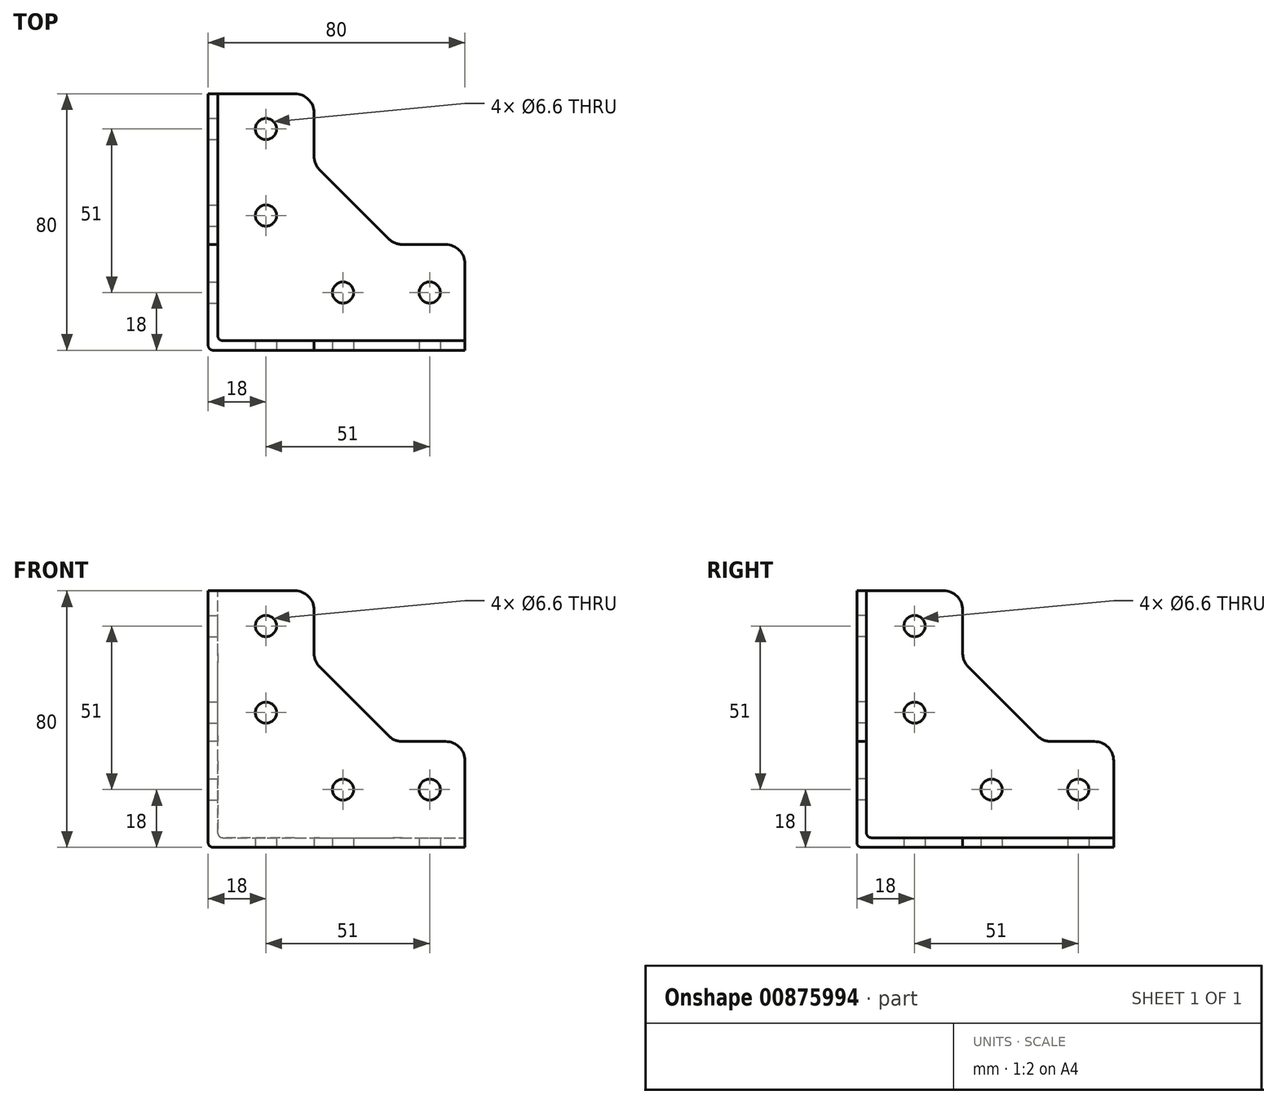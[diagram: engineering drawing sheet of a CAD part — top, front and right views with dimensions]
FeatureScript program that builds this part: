
annotation { "Feature Type Name" : "Feature", "Feature Type Description" : "" }
export const myFeature = defineFeature(function(context is Context, id is Id, definition is map)
    precondition{}
    {
        {
            var Q0;
            Q0=qCreatedBy(makeId("Front.planeOp"),FACE);
            var sketch = newSketch(context, id + "F0", { "sketchPlane" : qUnion([Q0])});
            skLineSegment(sketch, "E0", {"start": v(0, 80) * mm, "end": v(0, 0) * mm});
            skLineSegment(sketch, "E1", {"start": v(0, 0) * mm, "end": v(80, 0) * mm});
            skLineSegment(sketch, "E2", {"start": v(80, 0) * mm, "end": v(80, 33) * mm});
            skLineSegment(sketch, "E3", {"start": v(33, 80) * mm, "end": v(0, 80) * mm});
            skLineSegment(sketch, "E4", {"start": v(80, 33) * mm, "end": v(58, 33) * mm});
            skLineSegment(sketch, "E5", {"start": v(58, 33) * mm, "end": v(33, 58) * mm});
            skLineSegment(sketch, "E6", {"start": v(33, 58) * mm, "end": v(33, 80) * mm});
            skSolve(sketch);
        }
        {
            var Q0;
            Q0 = qSketchRegion(id + "F0", true);
            extrude(context, id + "F1", {"entities" : qUnion([Q0]), "oppositeDirection" : true, "depth" : 3 * mm, "offsetDistance" : 25 * mm});
        }
        {
            var Q0;
            Q0=qCreatedBy(makeId("Right.planeOp"),FACE);
            var sketch = newSketch(context, id + "F2", { "sketchPlane" : qUnion([Q0])});
            skLineSegment(sketch, "E7", {"start": v(0, 0) * mm, "end": v(0, 80) * mm});
            skLineSegment(sketch, "E8", {"start": v(0, 80) * mm, "end": v(33, 80) * mm});
            skLineSegment(sketch, "E9", {"start": v(80, 33) * mm, "end": v(80, 0) * mm});
            skLineSegment(sketch, "E10", {"start": v(80, 0) * mm, "end": v(0, 0) * mm});
            skLineSegment(sketch, "E11", {"start": v(80, 33) * mm, "end": v(58, 33) * mm});
            skLineSegment(sketch, "E12", {"start": v(58, 33) * mm, "end": v(33, 58) * mm});
            skLineSegment(sketch, "E13", {"start": v(33, 58) * mm, "end": v(33, 80) * mm});
            skSolve(sketch);
        }
        {
            var Q0;
            Q0 = qSketchRegion(id + "F2", true);
            extrude(context, id + "F3", {"entities" : qUnion([Q0]), "operationType" : NewBodyOperationType.ADD, "depth" : 3 * mm, "offsetDistance" : 25 * mm});
        }
        {
            var Q0;
            Q0=makeQuery(id+"F3.boolean.opBoolean","MERGE",FACE,{"derivedFrom":[makeQuery(id+"F1.opExtrude","SWEPT_FACE",FACE,{"disambiguationData":[OSD([sQuery(id+"F0.wireOp",EDGE,"E1")])]}),makeQuery(id+"F3.opExtrude","SWEPT_FACE",FACE,{"disambiguationData":[OSD([sQuery(id+"F2.wireOp",EDGE,"xK7a5ISh-bIRp-c4a8-oJV0-LNm0MhKTAAZs")])]})]});
            var sketch = newSketch(context, id + "F4", { "sketchPlane" : qUnion([Q0])});
            skLineSegment(sketch, "E14", {"start": v(0, 0) * mm, "end": v(80, 0) * mm});
            skLineSegment(sketch, "E15", {"start": v(80, 0) * mm, "end": v(80, -33) * mm});
            skLineSegment(sketch, "E16", {"start": v(33, -80) * mm, "end": v(0, -80) * mm});
            skLineSegment(sketch, "E17", {"start": v(0, -80) * mm, "end": v(0, 0) * mm});
            skLineSegment(sketch, "E18", {"start": v(33, -80) * mm, "end": v(33, -58) * mm});
            skLineSegment(sketch, "E19", {"start": v(33, -58) * mm, "end": v(58, -33) * mm});
            skLineSegment(sketch, "E20", {"start": v(58, -33) * mm, "end": v(80, -33) * mm});
            skSolve(sketch);
        }
        {
            var Q0;
            Q0 = qSketchRegion(id + "F4", true);
            extrude(context, id + "F5", {"entities" : qUnion([Q0]), "operationType" : NewBodyOperationType.ADD, "oppositeDirection" : true, "depth" : 3 * mm, "offsetDistance" : 25 * mm});
        }
        {
            var Q0;
            Q0=makeQuery(id+"F1.opExtrude","CAP_FACE",FACE,{"disambiguationData":[OSD([sQuery(id+"F0.wireOp",EDGE,"E0"),sQuery(id+"F0.wireOp",EDGE,"E1"),sQuery(id+"F0.wireOp",EDGE,"E2"),sQuery(id+"F0.wireOp",EDGE,"PdstRRKM-6kGl-S3Kn-xvEP-UkvPPowbuID2"),sQuery(id+"F0.wireOp",EDGE,"E3")])],"isStart":true});
            var sketch = newSketch(context, id + "F6", { "sketchPlane" : qUnion([Q0])});
            skLineSegment(sketch, "E21", {"start": v(80, 18) * mm, "end": v(80, 0) * mm, "construction": true});
            skLineSegment(sketch, "E22", {"start": v(0, 18) * mm, "end": v(42, 18) * mm, "construction": true});
            skLineSegment(sketch, "E23", {"start": v(42, 18) * mm, "end": v(69, 18) * mm, "construction": true});
            skLineSegment(sketch, "E24", {"start": v(69, 18) * mm, "end": v(80, 18) * mm, "construction": true});
            skLineSegment(sketch, "E25", {"start": v(0, 80) * mm, "end": v(18, 80) * mm, "construction": true});
            skLineSegment(sketch, "E26", {"start": v(18, 80) * mm, "end": v(18, 0) * mm, "construction": true});
            skPoint(sketch, "E27", {"position": v(18, 69) * mm});
            skPoint(sketch, "E28", {"position": v(18, 42) * mm});
            skSolve(sketch);
        }
        {
            var Q0;
            Q0=sQuery(id+"F6.wireOp",VERTEX,"E22.end");
            var Q1;
            Q1=sQuery(id+"F6.wireOp",VERTEX,"E23.end");
            var Q2;
            Q2=sQuery(id+"F6.wireOp",VERTEX,"E27");
            var Q3;
            Q3=sQuery(id+"F6.wireOp",VERTEX,"E28");
            var Q4;
            Q4=makeQuery(id+"F1.opExtrude","SWEPT_BODY",BODY,{"disambiguationData":[OSD([sQuery(id+"F0.wireOp",EDGE,"E0"),sQuery(id+"F0.wireOp",EDGE,"E1"),sQuery(id+"F0.wireOp",EDGE,"E2"),sQuery(id+"F0.wireOp",EDGE,"PdstRRKM-6kGl-S3Kn-xvEP-UkvPPowbuID2"),sQuery(id+"F0.wireOp",EDGE,"E3")])]});
            hole(context, id + "F7", {"style" : HoleStyle.SIMPLE, "endStyle" : HoleEndStyle.THROUGH, "standardTappedOrClearance" : lookupTablePath({ "fit" : "Normal", "standard" : "ISO", "size" : "M6", "type" : "Clearance" }), "standardBlindInLast" : lookupTablePath({ "fit" : "Normal", "standard" : "ISO", "size" : "M6", "type" : "Clearance" }), "holeDiameter" : 6.6 * mm, "majorDiameter" : 5 * mm, "isTappedThrough" : true, "tappedDepth" : 18.5 * mm, "tapClearance" : 3, "locations" : qUnion([Q0, Q1, Q2, Q3]), "scope" : qUnion([Q4])});
        }
        {
            var Q0;
            Q0=makeQuery(id+"F3.opExtrude","CAP_FACE",FACE,{"disambiguationData":[OSD([sQuery(id+"F2.wireOp",EDGE,"E7"),sQuery(id+"F2.wireOp",EDGE,"E8"),sQuery(id+"F2.wireOp",EDGE,"zJ48BfmZ-ECgL-81z3-b86R-i4EXetppoDrJ"),sQuery(id+"F2.wireOp",EDGE,"E9"),sQuery(id+"F2.wireOp",EDGE,"E10")])],"isStart":false});
            var sketch = newSketch(context, id + "F8", { "sketchPlane" : qUnion([Q0])});
            skLineSegment(sketch, "E29", {"start": v(80, 18) * mm, "end": v(80, 0) * mm, "construction": true});
            skLineSegment(sketch, "E30", {"start": v(0, 18) * mm, "end": v(42, 18) * mm, "construction": true});
            skLineSegment(sketch, "E31", {"start": v(42, 18) * mm, "end": v(69, 18) * mm, "construction": true});
            skLineSegment(sketch, "E32", {"start": v(69, 18) * mm, "end": v(80, 18) * mm, "construction": true});
            skLineSegment(sketch, "E33", {"start": v(0, 80) * mm, "end": v(18, 80) * mm, "construction": true});
            skLineSegment(sketch, "E34", {"start": v(18, 80) * mm, "end": v(18, 0) * mm, "construction": true});
            skPoint(sketch, "E35", {"position": v(18, 80) * mm});
            skPoint(sketch, "E36", {"position": v(18, 69) * mm});
            skPoint(sketch, "E37", {"position": v(18, 42) * mm});
            skSolve(sketch);
        }
        {
            var Q0;
            Q0=sQuery(id+"F8.wireOp",VERTEX,"E30.end");
            var Q1;
            Q1=sQuery(id+"F8.wireOp",VERTEX,"E31.end");
            var Q2;
            Q2=sQuery(id+"F8.wireOp",VERTEX,"E36");
            var Q3;
            Q3=sQuery(id+"F8.wireOp",VERTEX,"E37");
            var Q4;
            Q4=makeQuery(id+"F1.opExtrude","SWEPT_BODY",BODY,{"disambiguationData":[OSD([sQuery(id+"F0.wireOp",EDGE,"E0"),sQuery(id+"F0.wireOp",EDGE,"E1"),sQuery(id+"F0.wireOp",EDGE,"E2"),sQuery(id+"F0.wireOp",EDGE,"PdstRRKM-6kGl-S3Kn-xvEP-UkvPPowbuID2"),sQuery(id+"F0.wireOp",EDGE,"E3")])]});
            hole(context, id + "F9", {"style" : HoleStyle.SIMPLE, "endStyle" : HoleEndStyle.THROUGH, "standardTappedOrClearance" : lookupTablePath({ "fit" : "Normal", "standard" : "ISO", "size" : "M6", "type" : "Clearance" }), "standardBlindInLast" : lookupTablePath({ "fit" : "Normal", "standard" : "ISO", "size" : "M6", "type" : "Clearance" }), "holeDiameter" : 6.6 * mm, "majorDiameter" : 5 * mm, "isTappedThrough" : true, "tappedDepth" : 18.5 * mm, "tapClearance" : 3, "locations" : qUnion([Q0, Q1, Q2, Q3]), "scope" : qUnion([Q4])});
        }
        {
            var Q0;
            Q0=makeQuery(id+"F5.boolean.opBoolean","MERGE",FACE,{"derivedFrom":[makeQuery(id+"F3.boolean.opBoolean","MERGE",FACE,{"derivedFrom":[makeQuery(id+"F1.opExtrude","SWEPT_FACE",FACE,{"disambiguationData":[OSD([sQuery(id+"F0.wireOp",EDGE,"E1")])]}),makeQuery(id+"F3.opExtrude","SWEPT_FACE",FACE,{"disambiguationData":[OSD([sQuery(id+"F2.wireOp",EDGE,"E10")])]})]}),makeQuery(id+"F5.opExtrude","CAP_FACE",FACE,{"disambiguationData":[OSD([sQuery(id+"F4.wireOp",EDGE,"E14"),sQuery(id+"F4.wireOp",EDGE,"E15"),sQuery(id+"F4.wireOp",EDGE,"mDaul06L-Xs64-WxXX-hdnx-pq6gpseUhkKR"),sQuery(id+"F4.wireOp",EDGE,"E16"),sQuery(id+"F4.wireOp",EDGE,"E17")])],"isStart":true})]});
            var sketch = newSketch(context, id + "F10", { "sketchPlane" : qUnion([Q0])});
            skLineSegment(sketch, "E38", {"start": v(18, 0) * mm, "end": v(18, -80) * mm, "construction": true});
            skPoint(sketch, "E39", {"position": v(18, -69) * mm});
            skPoint(sketch, "E40", {"position": v(18, -42) * mm});
            skLineSegment(sketch, "E41", {"start": v(18, -80) * mm, "end": v(0, -80) * mm, "construction": true});
            skLineSegment(sketch, "E42", {"start": v(0, -18) * mm, "end": v(80, -18) * mm, "construction": true});
            skLineSegment(sketch, "E43", {"start": v(80, -18) * mm, "end": v(80, 0) * mm, "construction": true});
            skPoint(sketch, "E44", {"position": v(69, -18) * mm});
            skPoint(sketch, "E45", {"position": v(42, -18) * mm});
            skSolve(sketch);
        }
        {
            var Q0;
            Q0=sQuery(id+"F10.wireOp",VERTEX,"E45");
            var Q1;
            Q1=sQuery(id+"F10.wireOp",VERTEX,"E44");
            var Q2;
            Q2=sQuery(id+"F10.wireOp",VERTEX,"E40");
            var Q3;
            Q3=sQuery(id+"F10.wireOp",VERTEX,"E39");
            var Q4;
            Q4=makeQuery(id+"F1.opExtrude","SWEPT_BODY",BODY,{"disambiguationData":[OSD([sQuery(id+"F0.wireOp",EDGE,"E0"),sQuery(id+"F0.wireOp",EDGE,"E1"),sQuery(id+"F0.wireOp",EDGE,"E2"),sQuery(id+"F0.wireOp",EDGE,"PdstRRKM-6kGl-S3Kn-xvEP-UkvPPowbuID2"),sQuery(id+"F0.wireOp",EDGE,"E3")])]});
            hole(context, id + "F11", {"style" : HoleStyle.SIMPLE, "endStyle" : HoleEndStyle.THROUGH, "standardTappedOrClearance" : lookupTablePath({ "fit" : "Normal", "standard" : "ISO", "size" : "M6", "type" : "Clearance" }), "standardBlindInLast" : lookupTablePath({ "fit" : "Normal", "standard" : "ISO", "size" : "M6", "type" : "Clearance" }), "holeDiameter" : 6.6 * mm, "majorDiameter" : 5 * mm, "isTappedThrough" : true, "tappedDepth" : 18.5 * mm, "tapClearance" : 3, "locations" : qUnion([Q0, Q1, Q2, Q3]), "scope" : qUnion([Q4])});
        }
        {
            var Q0;
            Q0=makeQuery(id+"F1.opExtrude","SWEPT_EDGE",EDGE,{"disambiguationData":[OSD([sQuery(id+"F0.wireOp",EDGE,"E3"),sQuery(id+"F0.wireOp",EDGE,"E6")])]});
            var Q1;
            Q1=makeQuery(id+"F3.opExtrude","SWEPT_EDGE",EDGE,{"disambiguationData":[OSD([sQuery(id+"F2.wireOp",EDGE,"E9"),sQuery(id+"F2.wireOp",EDGE,"E11")])]});
            var Q2;
            Q2=makeQuery(id+"F1.opExtrude","SWEPT_EDGE",EDGE,{"disambiguationData":[OSD([sQuery(id+"F0.wireOp",EDGE,"E2"),sQuery(id+"F0.wireOp",EDGE,"E4")])]});
            var Q3;
            Q3=makeQuery(id+"F1.opExtrude","SWEPT_EDGE",EDGE,{"disambiguationData":[OSD([sQuery(id+"F0.wireOp",EDGE,"E5"),sQuery(id+"F0.wireOp",EDGE,"E6")])]});
            var Q4;
            Q4=makeQuery(id+"F1.opExtrude","SWEPT_EDGE",EDGE,{"disambiguationData":[OSD([sQuery(id+"F0.wireOp",EDGE,"E4"),sQuery(id+"F0.wireOp",EDGE,"E5")])]});
            var Q5;
            Q5=makeQuery(id+"F5.opExtrude","SWEPT_EDGE",EDGE,{"disambiguationData":[OSD([sQuery(id+"F4.wireOp",EDGE,"E19"),sQuery(id+"F4.wireOp",EDGE,"E20")])]});
            var Q6;
            Q6=makeQuery(id+"F5.opExtrude","SWEPT_EDGE",EDGE,{"disambiguationData":[OSD([sQuery(id+"F4.wireOp",EDGE,"E18"),sQuery(id+"F4.wireOp",EDGE,"E19")])]});
            var Q7;
            Q7=makeQuery(id+"F3.opExtrude","SWEPT_EDGE",EDGE,{"disambiguationData":[OSD([sQuery(id+"F2.wireOp",EDGE,"E11"),sQuery(id+"F2.wireOp",EDGE,"E12")])]});
            var Q8;
            Q8=makeQuery(id+"F3.opExtrude","SWEPT_EDGE",EDGE,{"disambiguationData":[OSD([sQuery(id+"F2.wireOp",EDGE,"E12"),sQuery(id+"F2.wireOp",EDGE,"E13")])]});
            var Q9;
            Q9=makeQuery(id+"F3.opExtrude","SWEPT_EDGE",EDGE,{"disambiguationData":[OSD([sQuery(id+"F2.wireOp",EDGE,"E8"),sQuery(id+"F2.wireOp",EDGE,"E13")])]});
            var Q10;
            Q10=makeQuery(id+"F5.opExtrude","SWEPT_EDGE",EDGE,{"disambiguationData":[OSD([sQuery(id+"F4.wireOp",EDGE,"E16"),sQuery(id+"F4.wireOp",EDGE,"E18")])]});
            var Q11;
            Q11=makeQuery(id+"F5.opExtrude","SWEPT_EDGE",EDGE,{"disambiguationData":[OSD([sQuery(id+"F4.wireOp",EDGE,"E15"),sQuery(id+"F4.wireOp",EDGE,"E20")])]});
            fillet(context, id + "F12", {"entities" : qUnion([Q0, Q1, Q2, Q3, Q4, Q5, Q6, Q7, Q8, Q9, Q10, Q11]), "radius" : 6 * mm, "tangentPropagation" : true, "allowEdgeOverflow" : false});
        }
        {
            var Q0;
            Q0=makeQuery(id+"F5.boolean.opBoolean","INTERSECT",EDGE,{"derivedFrom":[makeQuery(id+"F1.opExtrude","CAP_FACE",FACE,{"disambiguationData":[OSD([sQuery(id+"F0.wireOp",EDGE,"E0"),sQuery(id+"F0.wireOp",EDGE,"E1"),sQuery(id+"F0.wireOp",EDGE,"E2"),sQuery(id+"F0.wireOp",EDGE,"PdstRRKM-6kGl-S3Kn-xvEP-UkvPPowbuID2"),sQuery(id+"F0.wireOp",EDGE,"E3")])],"isStart":false}),makeQuery(id+"F5.opExtrude","CAP_FACE",FACE,{"disambiguationData":[OSD([sQuery(id+"F4.wireOp",EDGE,"E14"),sQuery(id+"F4.wireOp",EDGE,"E15"),sQuery(id+"F4.wireOp",EDGE,"mDaul06L-Xs64-WxXX-hdnx-pq6gpseUhkKR"),sQuery(id+"F4.wireOp",EDGE,"E16"),sQuery(id+"F4.wireOp",EDGE,"E17")])],"isStart":false})]});
            var Q1;
            Q1=makeQuery(id+"F5.boolean.opBoolean","INTERSECT",EDGE,{"derivedFrom":[makeQuery(id+"F3.opExtrude","CAP_FACE",FACE,{"disambiguationData":[OSD([sQuery(id+"F2.wireOp",EDGE,"E7"),sQuery(id+"F2.wireOp",EDGE,"E8"),sQuery(id+"F2.wireOp",EDGE,"zJ48BfmZ-ECgL-81z3-b86R-i4EXetppoDrJ"),sQuery(id+"F2.wireOp",EDGE,"E9"),sQuery(id+"F2.wireOp",EDGE,"E10")])],"isStart":false}),makeQuery(id+"F5.opExtrude","CAP_FACE",FACE,{"disambiguationData":[OSD([sQuery(id+"F4.wireOp",EDGE,"E14"),sQuery(id+"F4.wireOp",EDGE,"E15"),sQuery(id+"F4.wireOp",EDGE,"mDaul06L-Xs64-WxXX-hdnx-pq6gpseUhkKR"),sQuery(id+"F4.wireOp",EDGE,"E16"),sQuery(id+"F4.wireOp",EDGE,"E17")])],"isStart":false})]});
            var Q2;
            Q2=makeQuery(id+"F3.boolean.opBoolean","INTERSECT",EDGE,{"derivedFrom":[makeQuery(id+"F1.opExtrude","CAP_FACE",FACE,{"disambiguationData":[OSD([sQuery(id+"F0.wireOp",EDGE,"E0"),sQuery(id+"F0.wireOp",EDGE,"E1"),sQuery(id+"F0.wireOp",EDGE,"E2"),sQuery(id+"F0.wireOp",EDGE,"PdstRRKM-6kGl-S3Kn-xvEP-UkvPPowbuID2"),sQuery(id+"F0.wireOp",EDGE,"E3")])],"isStart":false}),makeQuery(id+"F3.opExtrude","CAP_FACE",FACE,{"disambiguationData":[OSD([sQuery(id+"F2.wireOp",EDGE,"E7"),sQuery(id+"F2.wireOp",EDGE,"E8"),sQuery(id+"F2.wireOp",EDGE,"zJ48BfmZ-ECgL-81z3-b86R-i4EXetppoDrJ"),sQuery(id+"F2.wireOp",EDGE,"E9"),sQuery(id+"F2.wireOp",EDGE,"E10")])],"isStart":false})]});
            var Q3;
            Q3=makeQuery(id+"F1.opExtrude","CAP_EDGE",EDGE,{"disambiguationData":[OSD([sQuery(id+"F0.wireOp",EDGE,"E1")])],"isStart":true});
            var Q4;
            Q4=makeQuery(id+"F1.opExtrude","CAP_EDGE",EDGE,{"disambiguationData":[OSD([sQuery(id+"F0.wireOp",EDGE,"E0")])],"isStart":true});
            var Q5;
            Q5=makeQuery(id+"F3.boolean.opBoolean","MERGE",EDGE,{"derivedFrom":[makeQuery(id+"F1.opExtrude","SWEPT_EDGE",EDGE,{"disambiguationData":[OSD([sQuery(id+"F0.wireOp",EDGE,"E0"),sQuery(id+"F0.wireOp",EDGE,"E1")])]}),makeQuery(id+"F3.opExtrude","CAP_EDGE",EDGE,{"disambiguationData":[OSD([sQuery(id+"F2.wireOp",EDGE,"E10")])],"isStart":true})]});
            fillet(context, id + "F13", {"entities" : qUnion([Q0, Q1, Q2, Q3, Q4, Q5]), "radius" : 1.5 * mm, "allowEdgeOverflow" : false});
        }
    });
